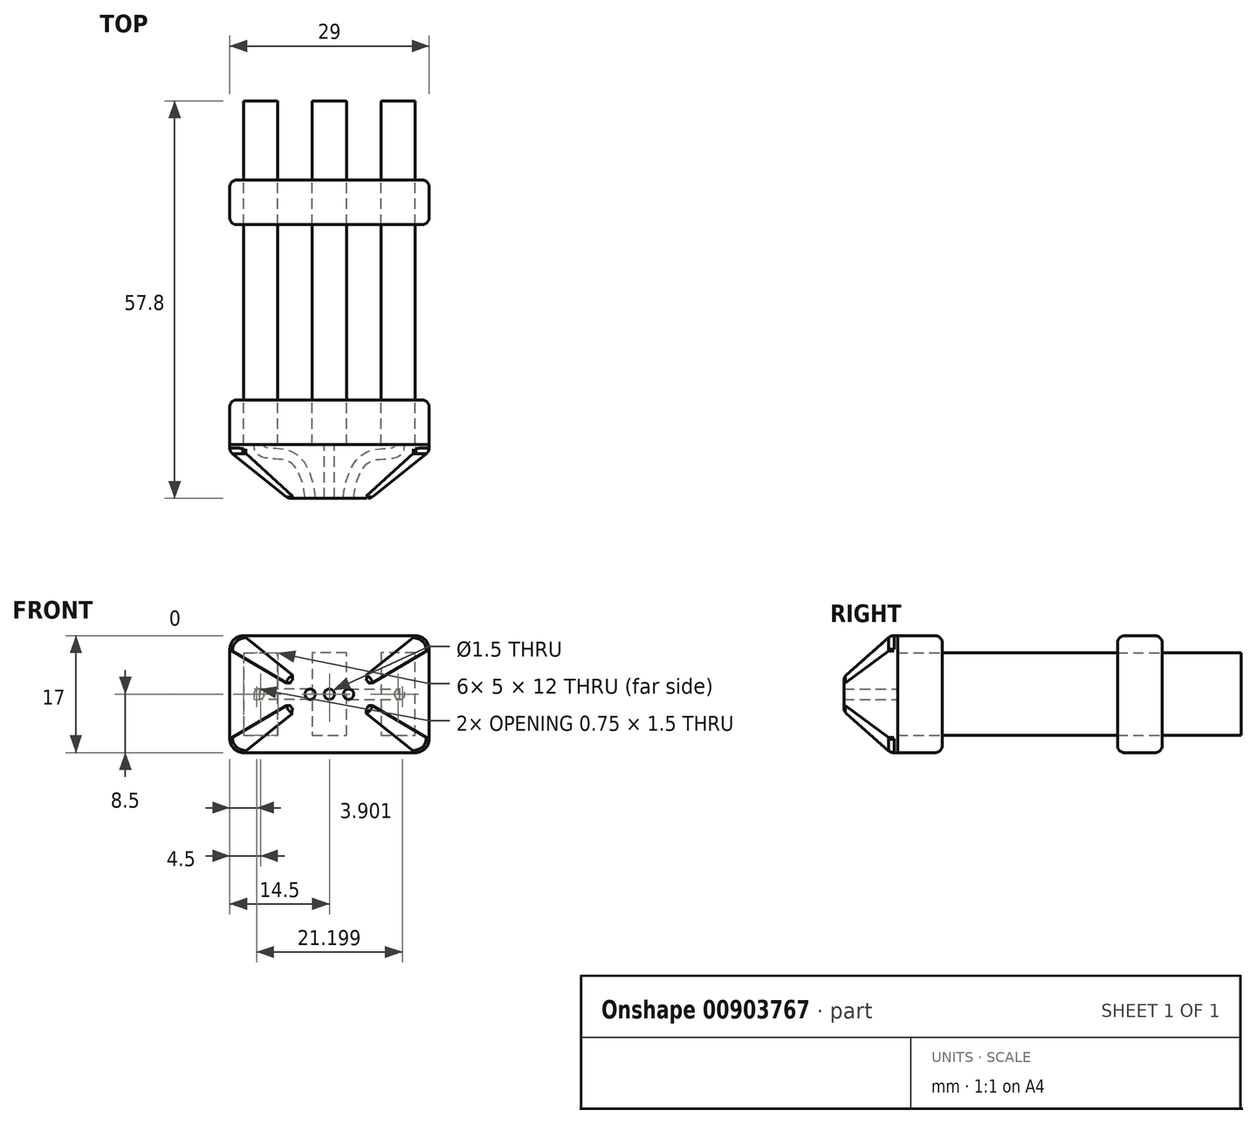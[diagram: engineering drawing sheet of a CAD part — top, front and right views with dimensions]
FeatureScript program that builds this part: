
annotation { "Feature Type Name" : "Feature", "Feature Type Description" : "" }
export const myFeature = defineFeature(function(context is Context, id is Id, definition is map)
    precondition{}
    {
        {
            var Q0;
            Q0=qCreatedBy(makeId("Front.planeOp"),FACE);
            var sketch = newSketch(context, id + "F0", { "sketchPlane" : qUnion([Q0])});
            skLineSegment(sketch, "E0.bottom", {"start": v(0, 0) * mm, "end": v(5, 0) * mm});
            skLineSegment(sketch, "E0.top", {"start": v(0, 12) * mm, "end": v(5, 12) * mm});
            skLineSegment(sketch, "E0.left", {"start": v(0, 0) * mm, "end": v(0, 12) * mm});
            skLineSegment(sketch, "E0.right", {"start": v(5, 0) * mm, "end": v(5, 12) * mm});
            skLineSegment(sketch, "E1.1.0.0", {"start": v(10, 0) * mm, "end": v(10, 12) * mm});
            skLineSegment(sketch, "E1.1.0.1", {"start": v(15, 0) * mm, "end": v(15, 12) * mm});
            skLineSegment(sketch, "E1.1.0.2", {"start": v(10, 12) * mm, "end": v(15, 12) * mm});
            skLineSegment(sketch, "E1.1.0.3", {"start": v(10, 0) * mm, "end": v(15, 0) * mm});
            skLineSegment(sketch, "E1.2.0.0", {"start": v(20, 0) * mm, "end": v(20, 12) * mm});
            skLineSegment(sketch, "E1.2.0.1", {"start": v(25, 0) * mm, "end": v(25, 12) * mm});
            skLineSegment(sketch, "E1.2.0.2", {"start": v(20, 12) * mm, "end": v(25, 12) * mm});
            skLineSegment(sketch, "E1.2.0.3", {"start": v(20, 0) * mm, "end": v(25, 0) * mm});
            skLineSegment(sketch, "E1.direction1", {"start": v(0, 0) * mm, "end": v(10, 0) * mm, "construction": true});
            skSolve(sketch);
        }
        {
            var Q0;
            Q0=makeQuery(id+"F0.imprint","IMPRINT",FACE,{"disambiguationData":[TD([[makeQuery(id+"F0.imprint","IMPRINT",EDGE,{"derivedFrom":sQuery(id+"F0.wireOp",EDGE,"E0.bottom")}),1.0]])]});
            var Q1;
            Q1=makeQuery(id+"F0.imprint","IMPRINT",FACE,{"disambiguationData":[TD([[makeQuery(id+"F0.imprint","IMPRINT",EDGE,{"derivedFrom":sQuery(id+"F0.wireOp",EDGE,"E1.1.0.0")}),-1.0]])]});
            var Q2;
            Q2=makeQuery(id+"F0.imprint","IMPRINT",FACE,{"disambiguationData":[TD([[makeQuery(id+"F0.imprint","IMPRINT",EDGE,{"derivedFrom":sQuery(id+"F0.wireOp",EDGE,"E1.2.0.0")}),-1.0]])]});
            extrude(context, id + "F1", {"entities" : qUnion([Q0, Q1, Q2]), "depth" : 50 * mm, "offsetDistance" : 25 * mm});
        }
        {
            var Q0;
            Q0=qCreatedBy(makeId("Front.planeOp"),FACE);
            cPlane(context, id + "F2", {"entities" : qUnion([Q0]), "cplaneType" : CPlaneType.OFFSET, "offset" : 43.5 * mm, "width" : 150 * mm, "height" : 150 * mm});
        }
        {
            var Q0;
            Q0=qCreatedBy(id+"F2.planeOp",FACE);
            var sketch = newSketch(context, id + "F3", { "sketchPlane" : qUnion([Q0])});
            skLineSegment(sketch, "E2.bottom", {"start": v(-2, -2.5) * mm, "end": v(27, -2.5) * mm});
            skLineSegment(sketch, "E2.top", {"start": v(-2, 14.5) * mm, "end": v(27, 14.5) * mm});
            skLineSegment(sketch, "E2.left", {"start": v(-2, -2.5) * mm, "end": v(-2, 14.5) * mm});
            skLineSegment(sketch, "E2.right", {"start": v(27, -2.5) * mm, "end": v(27, 14.5) * mm});
            skLineSegment(sketch, "E3.0", {"start": v(0, 12) * mm, "end": v(5, 12) * mm});
            skLineSegment(sketch, "E4.0.0", {"start": v(5, 12) * mm, "end": v(0, 12) * mm});
            skLineSegment(sketch, "E4.0.1", {"start": v(0, 12) * mm, "end": v(0, 0) * mm});
            skLineSegment(sketch, "E4.0.2", {"start": v(0, 0) * mm, "end": v(5, 0) * mm});
            skLineSegment(sketch, "E4.0.3", {"start": v(5, 0) * mm, "end": v(5, 12) * mm});
            skLineSegment(sketch, "E5.0.0", {"start": v(10, 0) * mm, "end": v(15, 0) * mm});
            skLineSegment(sketch, "E5.0.1", {"start": v(15, 0) * mm, "end": v(15, 12) * mm});
            skLineSegment(sketch, "E5.0.2", {"start": v(15, 12) * mm, "end": v(10, 12) * mm});
            skLineSegment(sketch, "E5.0.3", {"start": v(10, 12) * mm, "end": v(10, 0) * mm});
            skLineSegment(sketch, "E6.0.0", {"start": v(20, 0) * mm, "end": v(25, 0) * mm});
            skLineSegment(sketch, "E6.0.1", {"start": v(25, 0) * mm, "end": v(25, 12) * mm});
            skLineSegment(sketch, "E6.0.2", {"start": v(25, 12) * mm, "end": v(20, 12) * mm});
            skLineSegment(sketch, "E6.0.3", {"start": v(20, 12) * mm, "end": v(20, 0) * mm});
            skPoint(sketch, "E7", {"position": v(12.5, 6) * mm});
            skPoint(sketch, "E7.positionSnap0", {"position": v(10, 6) * mm});
            skSolve(sketch);
        }
        {
            var Q0;
            Q0=makeQuery(id+"F3.imprint","IMPRINT",FACE,{"disambiguationData":[TD([[makeQuery(id+"F3.imprint","IMPRINT",EDGE,{"derivedFrom":sQuery(id+"F3.wireOp",EDGE,"E2.bottom")}),1.0]])]});
            var Q1;
            Q1=makeQuery(id+"F1.opExtrude","CAP_FACE",FACE,{"disambiguationData":[OSD([sQuery(id+"F0.wireOp",EDGE,"E0.bottom"),sQuery(id+"F0.wireOp",EDGE,"E0.top"),sQuery(id+"F0.wireOp",EDGE,"E0.left"),sQuery(id+"F0.wireOp",EDGE,"E0.right")])],"isStart":false});
            extrude(context, id + "F4", {"entities" : qUnion([Q0]), "endBound" : BoundingType.UP_TO_SURFACE, "depth" : 2.6 * mm, "endBoundEntityFace" : qUnion([Q1]), "offsetDistance" : 25 * mm});
        }
        {
            var Q0;
            Q0=makeQuery(id+"F4.opExtrude","SWEPT_BODY",BODY,{"disambiguationData":[OSD([sQuery(id+"F3.wireOp",EDGE,"E2.bottom"),sQuery(id+"F3.wireOp",EDGE,"E2.top"),sQuery(id+"F3.wireOp",EDGE,"E2.left"),sQuery(id+"F3.wireOp",EDGE,"E2.right"),sQuery(id+"F3.wireOp",EDGE,"E4.0.0"),sQuery(id+"F3.wireOp",EDGE,"E4.0.1"),sQuery(id+"F3.wireOp",EDGE,"E4.0.2"),sQuery(id+"F3.wireOp",EDGE,"E4.0.3"),sQuery(id+"F3.wireOp",EDGE,"E5.0.0"),sQuery(id+"F3.wireOp",EDGE,"E5.0.1"),sQuery(id+"F3.wireOp",EDGE,"E5.0.2"),sQuery(id+"F3.wireOp",EDGE,"E5.0.3"),sQuery(id+"F3.wireOp",EDGE,"E6.0.0"),sQuery(id+"F3.wireOp",EDGE,"E6.0.1"),sQuery(id+"F3.wireOp",EDGE,"E6.0.2"),sQuery(id+"F3.wireOp",EDGE,"E6.0.3")])]});
            transform(context, id + "F5", {"entities" : qUnion([Q0]), "transformType" : TransformType.TRANSLATION_3D, "dx" : 0 * mm, "dy" : 32 * mm, "dz" : 0 * mm, "makeCopy" : true});
        }
        {
            var Q0;
            Q0=makeQuery(id+"F4.opExtrude","SWEPT_EDGE",EDGE,{"disambiguationData":[OSD([sQuery(id+"F3.wireOp",EDGE,"E2.bottom"),sQuery(id+"F3.wireOp",EDGE,"E2.right")])]});
            var Q1;
            Q1=makeQuery(id+"F5.opPattern","COPY",EDGE,{"derivedFrom":makeQuery(id+"F4.opExtrude","SWEPT_EDGE",EDGE,{"disambiguationData":[OSD([sQuery(id+"F3.wireOp",EDGE,"E2.bottom"),sQuery(id+"F3.wireOp",EDGE,"E2.right")])]}),"instanceName":"1"});
            var Q2;
            Q2=makeQuery(id+"F5.opPattern","COPY",EDGE,{"derivedFrom":makeQuery(id+"F4.opExtrude","SWEPT_EDGE",EDGE,{"disambiguationData":[OSD([sQuery(id+"F3.wireOp",EDGE,"E2.bottom"),sQuery(id+"F3.wireOp",EDGE,"E2.left")])]}),"instanceName":"1"});
            var Q3;
            Q3=makeQuery(id+"F4.opExtrude","SWEPT_EDGE",EDGE,{"disambiguationData":[OSD([sQuery(id+"F3.wireOp",EDGE,"E2.bottom"),sQuery(id+"F3.wireOp",EDGE,"E2.left")])]});
            var Q4;
            Q4=makeQuery(id+"F5.opPattern","COPY",EDGE,{"derivedFrom":makeQuery(id+"F4.opExtrude","SWEPT_EDGE",EDGE,{"disambiguationData":[OSD([sQuery(id+"F3.wireOp",EDGE,"E2.top"),sQuery(id+"F3.wireOp",EDGE,"E2.right")])]}),"instanceName":"1"});
            var Q5;
            Q5=makeQuery(id+"F4.opExtrude","SWEPT_EDGE",EDGE,{"disambiguationData":[OSD([sQuery(id+"F3.wireOp",EDGE,"E2.top"),sQuery(id+"F3.wireOp",EDGE,"E2.right")])]});
            var Q6;
            Q6=makeQuery(id+"F5.opPattern","COPY",EDGE,{"derivedFrom":makeQuery(id+"F4.opExtrude","SWEPT_EDGE",EDGE,{"disambiguationData":[OSD([sQuery(id+"F3.wireOp",EDGE,"E2.top"),sQuery(id+"F3.wireOp",EDGE,"E2.left")])]}),"instanceName":"1"});
            var Q7;
            Q7=makeQuery(id+"F4.opExtrude","SWEPT_EDGE",EDGE,{"disambiguationData":[OSD([sQuery(id+"F3.wireOp",EDGE,"E2.top"),sQuery(id+"F3.wireOp",EDGE,"E2.left")])]});
            fillet(context, id + "F6", {"entities" : qUnion([Q0, Q1, Q2, Q3, Q4, Q5, Q6, Q7]), "radius" : 2 * mm, "tangentPropagation" : true, "allowEdgeOverflow" : false});
        }
        {
            var Q0;
            Q0=makeQuery(id+"F4.opExtrude","CAP_FACE",FACE,{"disambiguationData":[OSD([sQuery(id+"F3.wireOp",EDGE,"E2.bottom"),sQuery(id+"F3.wireOp",EDGE,"E2.top"),sQuery(id+"F3.wireOp",EDGE,"E2.left"),sQuery(id+"F3.wireOp",EDGE,"E2.right"),sQuery(id+"F3.wireOp",EDGE,"E4.0.0"),sQuery(id+"F3.wireOp",EDGE,"E4.0.1"),sQuery(id+"F3.wireOp",EDGE,"E4.0.2"),sQuery(id+"F3.wireOp",EDGE,"E4.0.3"),sQuery(id+"F3.wireOp",EDGE,"E5.0.0"),sQuery(id+"F3.wireOp",EDGE,"E5.0.1"),sQuery(id+"F3.wireOp",EDGE,"E5.0.2"),sQuery(id+"F3.wireOp",EDGE,"E5.0.3"),sQuery(id+"F3.wireOp",EDGE,"E6.0.0"),sQuery(id+"F3.wireOp",EDGE,"E6.0.1"),sQuery(id+"F3.wireOp",EDGE,"E6.0.2"),sQuery(id+"F3.wireOp",EDGE,"E6.0.3")])],"isStart":false});
            var sketch = newSketch(context, id + "F7", { "sketchPlane" : qUnion([Q0])});
            skLineSegment(sketch, "E8.0.0", {"start": v(25, 14.5) * mm, "end": v(0, 14.5) * mm});
            skArc(sketch, "E8.0.1", {"start": v(0, 14.5) * mm, "mid": v(-1.41, 13.91) * mm, "end": v(-2, 12.5) * mm});
            skLineSegment(sketch, "E8.0.2", {"start": v(-2, 12.5) * mm, "end": v(-2, -0.5) * mm});
            skArc(sketch, "E8.0.3", {"start": v(-2, -0.5) * mm, "mid": v(-1.41, -1.91) * mm, "end": v(0, -2.5) * mm});
            skLineSegment(sketch, "E8.0.4", {"start": v(0, -2.5) * mm, "end": v(25, -2.5) * mm});
            skArc(sketch, "E8.0.5", {"start": v(25, -2.5) * mm, "mid": v(26.41, -1.91) * mm, "end": v(27, -0.5) * mm});
            skLineSegment(sketch, "E8.0.6", {"start": v(27, -0.5) * mm, "end": v(27, 12.5) * mm});
            skArc(sketch, "E8.0.7", {"start": v(27, 12.5) * mm, "mid": v(26.41, 13.91) * mm, "end": v(25, 14.5) * mm});
            skSolve(sketch);
        }
        {
            var Q0;
            Q0=makeQuery(id+"F4.opExtrude","SWEPT_BODY",BODY,{"disambiguationData":[OSD([sQuery(id+"F3.wireOp",EDGE,"E2.bottom"),sQuery(id+"F3.wireOp",EDGE,"E2.top"),sQuery(id+"F3.wireOp",EDGE,"E2.left"),sQuery(id+"F3.wireOp",EDGE,"E2.right"),sQuery(id+"F3.wireOp",EDGE,"E4.0.0"),sQuery(id+"F3.wireOp",EDGE,"E4.0.1"),sQuery(id+"F3.wireOp",EDGE,"E4.0.2"),sQuery(id+"F3.wireOp",EDGE,"E4.0.3"),sQuery(id+"F3.wireOp",EDGE,"E5.0.0"),sQuery(id+"F3.wireOp",EDGE,"E5.0.1"),sQuery(id+"F3.wireOp",EDGE,"E5.0.2"),sQuery(id+"F3.wireOp",EDGE,"E5.0.3"),sQuery(id+"F3.wireOp",EDGE,"E6.0.0"),sQuery(id+"F3.wireOp",EDGE,"E6.0.1"),sQuery(id+"F3.wireOp",EDGE,"E6.0.2"),sQuery(id+"F3.wireOp",EDGE,"E6.0.3")])]});
            transform(context, id + "F8", {"entities" : qUnion([Q0]), "transformType" : TransformType.TRANSLATION_3D, "dx" : 0 * mm, "dy" : -14.3 * mm, "dz" : 0 * mm, "makeCopy" : true});
        }
        {
            var Q0;
            Q0=makeQuery(id+"F8.opPattern","COPY",EDGE,{"derivedFrom":makeQuery(id+"F4.opExtrude","CAP_EDGE",EDGE,{"disambiguationData":[OSD([sQuery(id+"F3.wireOp",EDGE,"E4.0.1")])],"isStart":false}),"instanceName":"1"});
            cPoint(context, id + "F9", {"entities" : qUnion([Q0]), "parameter" : 0.5});
        }
        {
            var Q0;
            Q0=makeQuery(id+"F8.opPattern","COPY",EDGE,{"derivedFrom":makeQuery(id+"F4.opExtrude","CAP_EDGE",EDGE,{"disambiguationData":[OSD([sQuery(id+"F3.wireOp",EDGE,"E6.0.1")])],"isStart":false}),"instanceName":"1"});
            cPoint(context, id + "F10", {"entities" : qUnion([Q0]), "parameter" : 0.5});
        }
        {
            var Q0;
            Q0=makeQuery(id+"F8.opPattern","COPY",EDGE,{"derivedFrom":makeQuery(id+"F4.opExtrude","CAP_EDGE",EDGE,{"disambiguationData":[OSD([sQuery(id+"F3.wireOp",EDGE,"E6.0.1")])],"isStart":true}),"instanceName":"1"});
            cPoint(context, id + "F11", {"entities" : qUnion([Q0]), "parameter" : 0.5});
        }
        {
            var Q0;
            Q0 = qCreatedBy(id + "F9" ,VERTEX);
            var Q1;
            Q1 = qCreatedBy(id + "F10" ,VERTEX);
            var Q2;
            Q2 = qCreatedBy(id + "F11" ,VERTEX);
            cPlane(context, id + "F12", {"entities" : qUnion([Q0, Q1, Q2]), "cplaneType" : CPlaneType.THREE_POINT, "offset" : 25 * mm, "width" : 150 * mm, "height" : 150 * mm});
        }
        {
            var Q0;
            Q0=qCreatedBy(id+"F12.planeOp",FACE);
            var sketch = newSketch(context, id + "F13", { "sketchPlane" : qUnion([Q0])});
            skPoint(sketch, "E9.0", {"position": v(12.5, 57.8) * mm});
            skPoint(sketch, "E10.0", {"position": v(12.5, 50) * mm});
            skLineSegment(sketch, "E11.0", {"start": v(0, 57.8) * mm, "end": v(25, 57.8) * mm, "construction": true});
            skLineSegment(sketch, "E12.0", {"start": v(0, 50) * mm, "end": v(25, 50) * mm, "construction": true});
            skFitSpline(sketch, "E13", {"points": [v(2.28, 50) * mm, v(6.97, 51.82) * mm, v(9.7, 57.8) * mm], "startDerivative": vector(-0.92, 12.46) * mm, "endDerivative": vector(0.1, 6.22) * mm});
            skLineSegment(sketch, "E14", {"start": v(12.5, 57.8) * mm, "end": v(12.5, 50) * mm});
            skFitSpline(sketch, "E15.MirrorCS", {"points": [v(22.72, 50) * mm, v(18.03, 51.82) * mm, v(15.3, 57.8) * mm], "startDerivative": vector(0.92, 12.46) * mm, "endDerivative": vector(-0.1, 6.22) * mm});
            skSolve(sketch);
        }
        {
            var Q0;
            Q0=makeQuery(id+"F8.opPattern","COPY",BODY,{"derivedFrom":makeQuery(id+"F4.opExtrude","SWEPT_BODY",BODY,{"disambiguationData":[OSD([sQuery(id+"F3.wireOp",EDGE,"E2.bottom"),sQuery(id+"F3.wireOp",EDGE,"E2.top"),sQuery(id+"F3.wireOp",EDGE,"E2.left"),sQuery(id+"F3.wireOp",EDGE,"E2.right"),sQuery(id+"F3.wireOp",EDGE,"E4.0.0"),sQuery(id+"F3.wireOp",EDGE,"E4.0.1"),sQuery(id+"F3.wireOp",EDGE,"E4.0.2"),sQuery(id+"F3.wireOp",EDGE,"E4.0.3"),sQuery(id+"F3.wireOp",EDGE,"E5.0.0"),sQuery(id+"F3.wireOp",EDGE,"E5.0.1"),sQuery(id+"F3.wireOp",EDGE,"E5.0.2"),sQuery(id+"F3.wireOp",EDGE,"E5.0.3"),sQuery(id+"F3.wireOp",EDGE,"E6.0.0"),sQuery(id+"F3.wireOp",EDGE,"E6.0.1"),sQuery(id+"F3.wireOp",EDGE,"E6.0.2"),sQuery(id+"F3.wireOp",EDGE,"E6.0.3")])]}),"instanceName":"1"});
            deleteBodies(context, id + "F14", {"entities" : qUnion([Q0])});
        }
        {
            var Q0;
            Q0=makeQuery(id+"F4.opExtrude","CAP_FACE",FACE,{"disambiguationData":[OSD([sQuery(id+"F3.wireOp",EDGE,"E2.bottom"),sQuery(id+"F3.wireOp",EDGE,"E2.top"),sQuery(id+"F3.wireOp",EDGE,"E2.left"),sQuery(id+"F3.wireOp",EDGE,"E2.right"),sQuery(id+"F3.wireOp",EDGE,"E4.0.0"),sQuery(id+"F3.wireOp",EDGE,"E4.0.1"),sQuery(id+"F3.wireOp",EDGE,"E4.0.2"),sQuery(id+"F3.wireOp",EDGE,"E4.0.3"),sQuery(id+"F3.wireOp",EDGE,"E5.0.0"),sQuery(id+"F3.wireOp",EDGE,"E5.0.1"),sQuery(id+"F3.wireOp",EDGE,"E5.0.2"),sQuery(id+"F3.wireOp",EDGE,"E5.0.3"),sQuery(id+"F3.wireOp",EDGE,"E6.0.0"),sQuery(id+"F3.wireOp",EDGE,"E6.0.1"),sQuery(id+"F3.wireOp",EDGE,"E6.0.2"),sQuery(id+"F3.wireOp",EDGE,"E6.0.3")])],"isStart":false});
            var Q1;
            Q1=sQuery(id+"F13.wireOp",VERTEX,"E9.0");
            cPlane(context, id + "F15", {"entities" : qUnion([Q0, Q1]), "cplaneType" : CPlaneType.PLANE_POINT, "offset" : 25 * mm, "width" : 150 * mm, "height" : 150 * mm});
        }
        {
            var Q0;
            Q0=qCreatedBy(id+"F15.planeOp",FACE);
            var sketch = newSketch(context, id + "F16", { "sketchPlane" : qUnion([Q0])});
            skPoint(sketch, "E16.0", {"position": v(12.5, 6) * mm});
            skLineSegment(sketch, "E17.bottom", {"start": v(7.5, 8.5) * mm, "end": v(17.5, 8.5) * mm});
            skLineSegment(sketch, "E17.top", {"start": v(7.5, 3.5) * mm, "end": v(17.5, 3.5) * mm});
            skLineSegment(sketch, "E17.left", {"start": v(6.5, 7.5) * mm, "end": v(6.5, 4.5) * mm});
            skLineSegment(sketch, "E17.right", {"start": v(18.5, 7.5) * mm, "end": v(18.5, 4.5) * mm});
            skPoint(sketch, "E18.visualSharp", {"position": v(6.5, 3.5) * mm});
            skArc(sketch, "E18.filletArc", {"start": v(6.5, 4.5) * mm, "mid": v(6.8, 3.8) * mm, "end": v(7.5, 3.5) * mm});
            skPoint(sketch, "E19.visualSharp", {"position": v(6.5, 8.5) * mm});
            skArc(sketch, "E19.filletArc", {"start": v(7.5, 8.5) * mm, "mid": v(6.8, 8.2) * mm, "end": v(6.5, 7.5) * mm});
            skPoint(sketch, "E20.visualSharp", {"position": v(18.5, 8.5) * mm});
            skArc(sketch, "E20.filletArc", {"start": v(18.5, 7.5) * mm, "mid": v(18.2, 8.2) * mm, "end": v(17.5, 8.5) * mm});
            skPoint(sketch, "E21.visualSharp", {"position": v(18.5, 3.5) * mm});
            skArc(sketch, "E21.filletArc", {"start": v(17.5, 3.5) * mm, "mid": v(18.2, 3.8) * mm, "end": v(18.5, 4.5) * mm});
            skSolve(sketch);
        }
        {
            var Q0;
            Q0 = qSketchRegion(id + "F7", true);
            extrude(context, id + "F17", {"entities" : qUnion([Q0]), "depth" : 1 * mm, "offsetDistance" : 25 * mm});
        }
        {
            var Q1;
            Q1=makeQuery(id+"F17.opExtrude","CAP_FACE",FACE,{"disambiguationData":[OSD([sQuery(id+"F7.wireOp",EDGE,"E8.0.0"),sQuery(id+"F7.wireOp",EDGE,"E8.0.1"),sQuery(id+"F7.wireOp",EDGE,"E8.0.2"),sQuery(id+"F7.wireOp",EDGE,"E8.0.3"),sQuery(id+"F7.wireOp",EDGE,"E8.0.4"),sQuery(id+"F7.wireOp",EDGE,"E8.0.5"),sQuery(id+"F7.wireOp",EDGE,"E8.0.6"),sQuery(id+"F7.wireOp",EDGE,"E8.0.7")])],"isStart":false});
            var Q2;
            Q2=makeQuery(id+"F16.imprint","IMPRINT",FACE,{"disambiguationData":[TD([[makeQuery(id+"F16.imprint","IMPRINT",EDGE,{"derivedFrom":sQuery(id+"F16.wireOp",EDGE,"E17.bottom")}),-1.0]])]});
            loft(context, id + "F18", {"operationType" : NewBodyOperationType.ADD, "sheetProfilesArray" : [{ "sheetProfileEntities" : qUnion([Q1]) }, { "sheetProfileEntities" : qUnion([Q2]) }]});
        }
        {
            var Q0;
            Q0=makeQuery(id+"F18.opLoft","CAP_FACE",FACE,{"disambiguationData":[OSD([makeQuery(id+"F16.imprint","IMPRINT",FACE,{"disambiguationData":[TD([[makeQuery(id+"F16.imprint","IMPRINT",EDGE,{"derivedFrom":sQuery(id+"F16.wireOp",EDGE,"E17.bottom")}),-1.0]])]})])],"isStart":true});
            var sketch = newSketch(context, id + "F19", { "sketchPlane" : qUnion([Q0])});
            skPoint(sketch, "E22.0", {"position": v(9.7, 6) * mm});
            skPoint(sketch, "E23.0", {"position": v(12.5, 6) * mm});
            skPoint(sketch, "E24.0", {"position": v(15.3, 6) * mm});
            skCircle(sketch, "E25", {"center": v(9.7, 6) * mm, "radius": 0.75 * mm});
            skCircle(sketch, "E26", {"center": v(12.5, 6) * mm, "radius": 0.75 * mm});
            skCircle(sketch, "E27", {"center": v(15.3, 6) * mm, "radius": 0.75 * mm});
            skSolve(sketch);
        }
        {
            var Q0;
            Q0=makeQuery(id+"F19.imprint","IMPRINT",FACE,{"disambiguationData":[TD([[makeQuery(id+"F19.imprint","IMPRINT",EDGE,{"derivedFrom":sQuery(id+"F19.wireOp",EDGE,"E25")}),1.0]])]});
            var Q1;
            Q1=sQuery(id+"F13.wireOp",EDGE,"E13");
            sweep(context, id + "F20", {"operationType" : NewBodyOperationType.REMOVE, "profiles" : qUnion([Q0]), "path" : qUnion([Q1])});
        }
        {
            var Q0;
            Q0=makeQuery(id+"F19.imprint","IMPRINT",FACE,{"disambiguationData":[TD([[makeQuery(id+"F19.imprint","IMPRINT",EDGE,{"derivedFrom":sQuery(id+"F19.wireOp",EDGE,"E27")}),1.0]])]});
            var Q1;
            Q1=sQuery(id+"F13.wireOp",EDGE,"E15.MirrorCS");
            sweep(context, id + "F21", {"operationType" : NewBodyOperationType.REMOVE, "profiles" : qUnion([Q0]), "path" : qUnion([Q1])});
        }
        {
            var Q0;
            Q0=makeQuery(id+"F19.imprint","IMPRINT",FACE,{"disambiguationData":[TD([[makeQuery(id+"F19.imprint","IMPRINT",EDGE,{"derivedFrom":sQuery(id+"F19.wireOp",EDGE,"E26")}),1.0]])]});
            var Q1;
            Q1=sQuery(id+"F13.wireOp",EDGE,"E14");
            sweep(context, id + "F22", {"operationType" : NewBodyOperationType.REMOVE, "profiles" : qUnion([Q0]), "path" : qUnion([Q1])});
        }
        {
            var Q0;
            Q0=makeQuery(id+"F5.opPattern","COPY",EDGE,{"derivedFrom":makeQuery(id+"F4.opExtrude","CAP_EDGE",EDGE,{"disambiguationData":[OSD([sQuery(id+"F3.wireOp",EDGE,"E2.bottom")])],"isStart":false}),"instanceName":"1"});
            var Q1;
            Q1=makeQuery(id+"F4.opExtrude","CAP_EDGE",EDGE,{"disambiguationData":[OSD([sQuery(id+"F3.wireOp",EDGE,"E2.top")])],"isStart":true});
            var Q2;
            Q2=makeQuery(id+"F5.opPattern","COPY",EDGE,{"derivedFrom":makeQuery(id+"F4.opExtrude","CAP_EDGE",EDGE,{"disambiguationData":[OSD([sQuery(id+"F3.wireOp",EDGE,"E2.top")])],"isStart":true}),"instanceName":"1"});
            var Q3;
            {var subQ0=sQuery(id+"F7.wireOp",EDGE,"E8.0.4");Q3=makeQuery(id+"F18.boolean.opBoolean","MERGE",EDGE,{"derivedFrom":[makeQuery(id+"F17.opExtrude","CAP_EDGE",EDGE,{"disambiguationData":[OSD([subQ0])],"isStart":false}),makeQuery(id+"F18.opLoft","MID_CAP_EDGE",EDGE,{"disambiguationData":[OSD([sQuery(id+"F7.wireOp",EDGE,"E8.0.3"),subQ0,sQuery(id+"F7.wireOp",EDGE,"E8.0.5")])],"capPos":0.0})]});}
            var Q4;
            Q4=makeQuery(id+"F18.opLoft","MID_CAP_EDGE",EDGE,{"disambiguationData":[OSD([sQuery(id+"F16.wireOp",EDGE,"E17.top"),sQuery(id+"F16.wireOp",EDGE,"E18.filletArc"),sQuery(id+"F16.wireOp",EDGE,"E21.filletArc")])],"capPos":1.0});
            fillet(context, id + "F23", {"entities" : qUnion([Q0, Q1, Q2, Q3, Q4]), "radius" : 1 * mm, "tangentPropagation" : true, "allowEdgeOverflow" : false});
        }
    });
